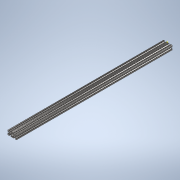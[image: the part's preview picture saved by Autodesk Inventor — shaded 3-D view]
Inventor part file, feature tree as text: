
AUTODESK INVENTOR PART (.ipt)
format: ipt  version: 2020 (Build 240168000, 168)  size: 360,448 bytes
history: native  units: in
note: dims shown in document units (in); Inventor stores cm internally (conversion verified against a paired STEP export)
features: sketch x2, extrude x1
ambient origin geometry x8: Origin, YZ Plane, XZ Plane, XY Plane, X Axis, Y Axis, Z Axis, Center Point
bodies: Solid1 (feature_tree)
feature tree (3):
  extrude  "Extrusion1"  [1 undecoded]
  sketch  "Sketch2"
  sketch  "Sketch1"  dims[d0=34.0in d1=0.0in]
note: 1 required parameter value undecoded (feature->parameter linkage not recoverable at this tier; creation-order binding heuristic only, values carry confidence <= 0.55)
